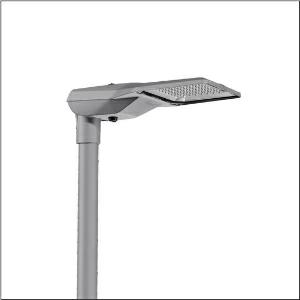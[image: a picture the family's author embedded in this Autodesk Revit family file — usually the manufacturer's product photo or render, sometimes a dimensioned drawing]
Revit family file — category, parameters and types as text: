
# Revit family: streetlight_sl_21_midi___st1_0ab_5xe3m33t08mb_b6c0
name_source: partatom
category: Lighting Fixtures
units: mm (PartAtom-declared; Revit-internal decimal feet)

## family parameters
Cut with Voids When Loaded = No
Host = Face
Light Source = No
Part Type = Normal
Room Calculation Point = No
Round Connector Dimension = Use Diameter
Shared = No

## types (1)
- --- (1 x LED, 16080 lm, 136 W, 3000K)
    Apparent Load = 136 VA
    CIE Flux Codes = 38 73 97 100 100
    Color Rendering = 70
    Color Temperature = 3000K
    Default Elevation = 1800 mm
    Description = Streetlight SL 21 midi, mast luminaire, primary light control with lens, of PMMA, primary optical cover: cover, of toughened safety glass, transparent, light distribution: ST1.0aB, light emission: direct distribution, primary light characteristic: asymmetric, installation type: side-entry, post-top, LED, High Power LED, rated luminous flux: 16.080lm, luminous efficacy: 118lm/W, light colour: 730, colour temperature: 3000K, control: flexible luminous flux parameterisation, time-dependent luminous flux control, constant luminous flux control, overheat protection, presetting dimming logarithmic, mains connection: 230..240V, AC, 50/60Hz, start of lifetime: 136W, end of service life: 142W, reduction: 61W, luminaire housing, of diecast aluminium, powder-coated, Siteco® metallic grey (DB 702S), corrosivity category C5 mid according to DIN EN ISO 12944, please order mast flange separately, inclination adjustable: 0°, 5°, 10°, 15°, sealing non-destructively replaceable, multi-level sealing system, length: 644mm, width: 335mm, height: 110mm, mast flange for spigot size: 42mm (side-entry): 5XC10008XM4, 60/48mm (side-entry/post-top): 5XC10108XM2, 76/60mm (side-entry/post-top): 5XC10108XM1, Smart Interface below and above, protection rating (complete): IP66, insulation class (complete): insulation class II (safety insulation), certification: CE, ENEC, ENEC+, VDE, impact resistance: IK09, permissible operating ambient temperature for outdoor applications: -40..+50°C, standard-compliant lighting for roads and squares, packaging unit: 1 piece

Light Distribution: ST1.0aB
    Height = 111 mm
    Lamp = 1 x LED
    Lamp Light Flux = 16080 lm
    Lamp Power = 136 W
    Lamp count = 1
    Length = 644 mm
    Luminous efficacy = 118 lm/W
    Manufacturer = Siteco
    ModVariant = No
    Model = 5XE3M33T08MB
    Number of Poles = 1
    OnlyDefault = Yes
    Power Factor = 1
    Product Name = Streetlight SL 21 midi | ST1.0aB
    Product group = mast luminaire | pylon top
    ProductGroupID = 6100
    Protection Class = Protection class II
    Protection Degree = IP 66
    RLX_Detail_Level = 1
    RLX_Emergency_Light_Flux = 0 lm
    RLX_Emergency_Type = 0
    RLX_Emergency_Type_DB = No
    RlxData = <blob elided: 90493 chars, md5=575fa267>
    Socket = socket
    Standby Power = 0 W
    System Light Flux = 16081 lm
    System Power = 136 W
    Type Comments = factory setting: luminous flux: 100 % | dim-lin: 254 | 695 mA
    Type Image = l_1004304.jpg
    URL = http://relux.com
    VarID = @adj_134329
    Voltage = 0 V
    Weight = 0.00 kg
    Width = 336 mm

## geometry (parser evidence)
native form markers: Blend x4, Sweep x12
no freeform markers — native parametric forms only
